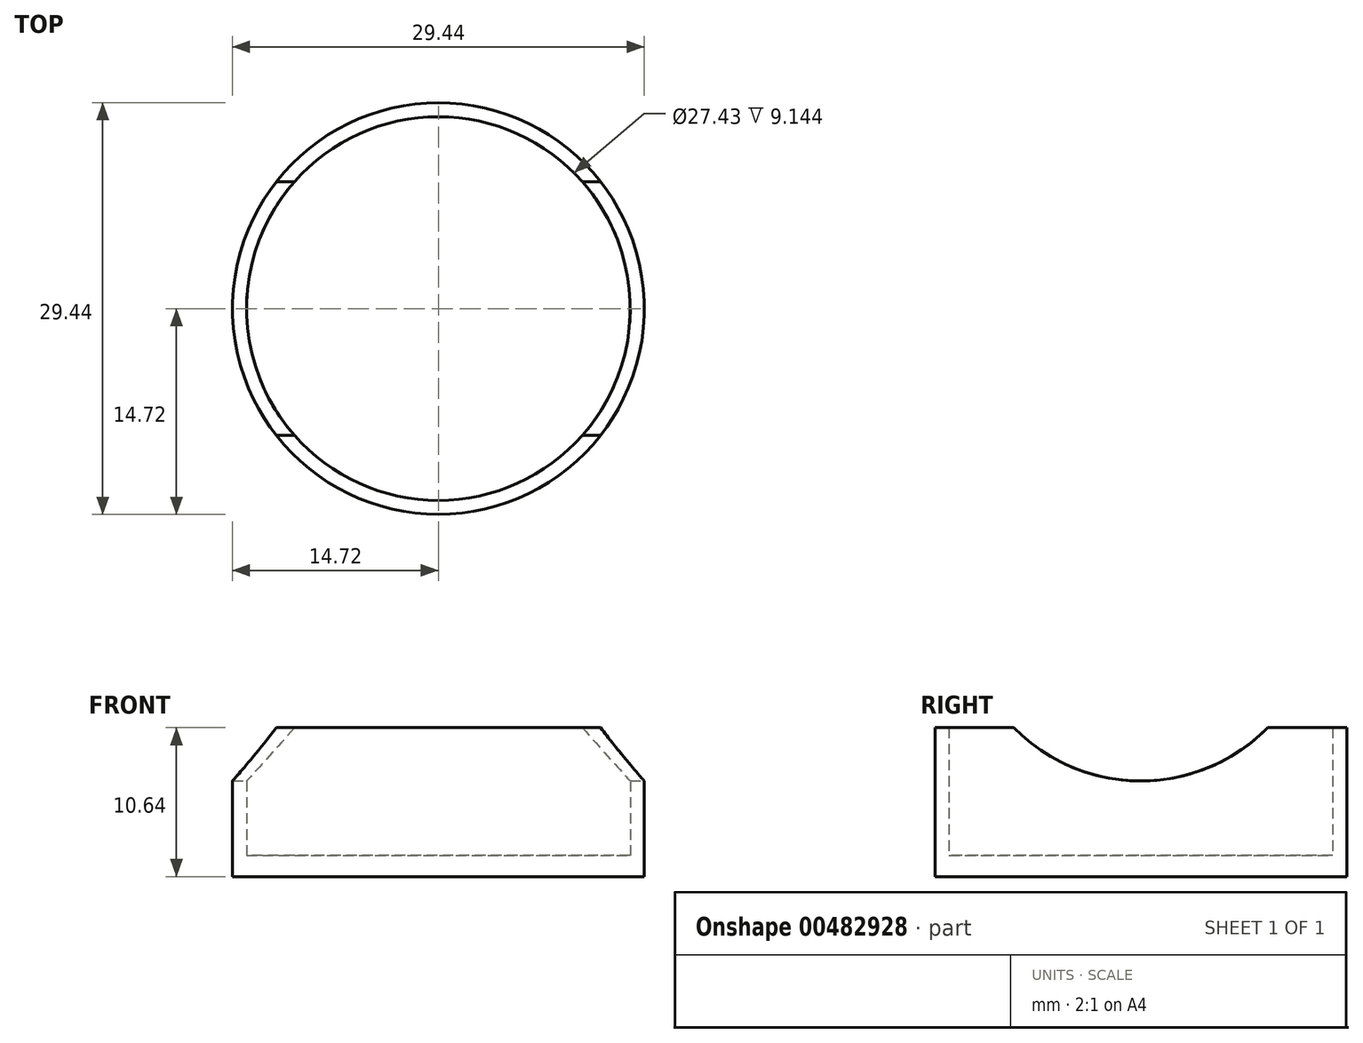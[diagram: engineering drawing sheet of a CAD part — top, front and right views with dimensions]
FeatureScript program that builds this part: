
annotation { "Feature Type Name" : "Feature", "Feature Type Description" : "" }
export const myFeature = defineFeature(function(context is Context, id is Id, definition is map)
    precondition{}
    {
        {
            assignVariable(context, id + "F0", {"name" : "t_base", "anyValue" : 1.5 * mm});
        }
        {
            assignVariable(context, id + "F1", {"name" : "h_board", "anyValue" : 7.87 * mm});
        }
        {
            var Q0;
            Q0=qCreatedBy(makeId("Top.planeOp"),FACE);
            var sketch = newSketch(context, id + "F2", { "sketchPlane" : qUnion([Q0])});
            skCircle(sketch, "E0", {"center": v(0, 0) * mm, "radius": 14.72 * mm});
            skSolve(sketch);
        }
        {
            var Q0;
            Q0 = qSketchRegion(id + "F2", true);
            extrude(context, id + "F3", {"entities" : qUnion([Q0]), "depth" : getVariable(context, 't_base'), "offsetDistance" : 25.4 * mm});
        }
        {
            var Q0;
            Q0=makeQuery(id+"F3.opExtrude","CAP_FACE",FACE,{"disambiguationData":[OSD([sQuery(id+"F2.wireOp",EDGE,"E0")])],"isStart":false});
            var sketch = newSketch(context, id + "F4", { "sketchPlane" : qUnion([Q0])});
            skCircle(sketch, "E1", {"center": v(0, 0) * mm, "radius": 13.72 * mm});
            skCircle(sketch, "E2", {"center": v(0, 0) * mm, "radius": 14.72 * mm});
            skSolve(sketch);
        }
        {
            var Q0;
            Q0 = qSketchRegion(id + "F4", true);
            extrude(context, id + "F5", {"entities" : qUnion([Q0]), "operationType" : NewBodyOperationType.ADD, "depth" : getVariable(context, 'h_board') + 1.27 * mm, "offsetDistance" : 25.4 * mm});
        }
        {
            var Q0;
            Q0=qCreatedBy(makeId("Right.planeOp"),FACE);
            var sketch = newSketch(context, id + "F6", { "sketchPlane" : qUnion([Q0])});
            skLineSegment(sketch, "E3", {"start": v(-15.47, 0) * mm, "end": v(20.58, 0) * mm, "construction": true});
            skLineSegment(sketch, "E4", {"start": v(-15.68, 10.64) * mm, "end": v(17.86, 10.64) * mm, "construction": true});
            skLineSegment(sketch, "E5", {"start": v(0, -0.27) * mm, "end": v(0, 18.93) * mm, "construction": true});
            skCircle(sketch, "E6", {"center": v(0, 19.53) * mm, "radius": 12.7 * mm});
            skLineSegment(sketch, "E7", {"start": v(-6.08, 6.83) * mm, "end": v(8.11, 6.83) * mm, "construction": true});
            skSolve(sketch);
        }
        {
            var Q0;
            Q0 = qSketchRegion(id + "F6", true);
            extrude(context, id + "F7", {"entities" : qUnion([Q0]), "operationType" : NewBodyOperationType.REMOVE, "endBound" : BoundingType.THROUGH_ALL, "oppositeDirection" : true, "depth" : 25.4 * mm, "offsetDistance" : 25.4 * mm, "hasSecondDirection" : true, "secondDirectionBound" : SecondDirectionBoundingType.THROUGH_ALL, "secondDirectionOppositeDirection" : false, "secondDirectionDepth" : 25.4 * mm});
        }
    });
